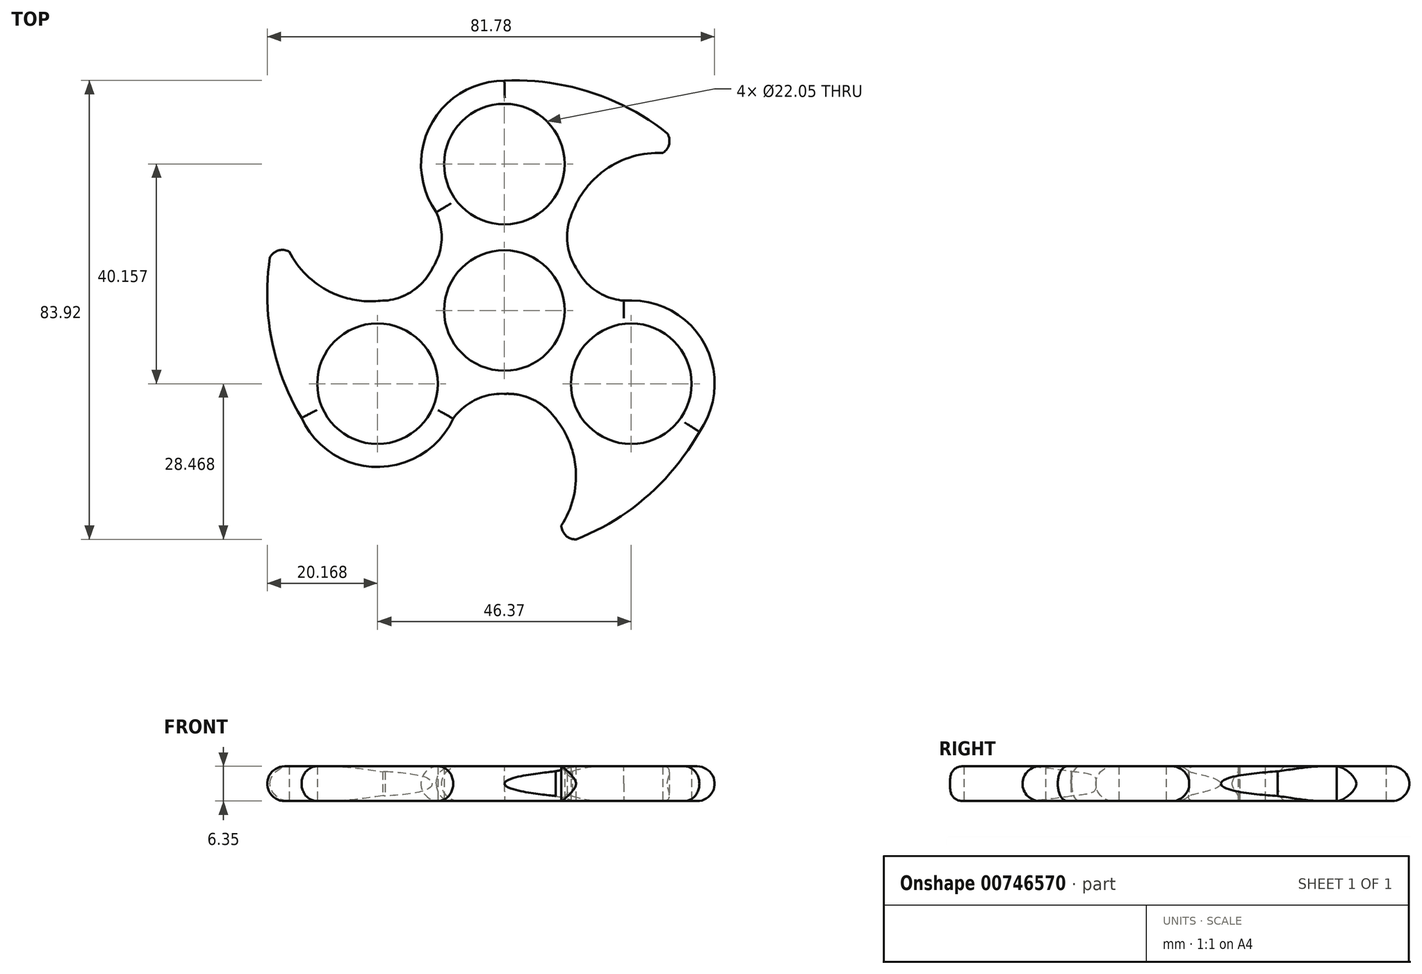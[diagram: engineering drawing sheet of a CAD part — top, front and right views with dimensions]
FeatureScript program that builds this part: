
annotation { "Feature Type Name" : "Feature", "Feature Type Description" : "" }
export const myFeature = defineFeature(function(context is Context, id is Id, definition is map)
    precondition{}
    {
        {
            var Q0;
            Q0=qCreatedBy(makeId("Top.planeOp"),FACE);
            var sketch = newSketch(context, id + "F0", { "sketchPlane" : qUnion([Q0])});
            skCircle(sketch, "E0", {"center": v(0, -0.08) * mm, "radius": 11.02 * mm});
            skCircle(sketch, "E1", {"center": v(0, -0.08) * mm, "radius": 15.24 * mm});
            skCircle(sketch, "E2", {"center": v(0, 26.7) * mm, "radius": 11.02 * mm});
            skCircle(sketch, "E3", {"center": v(0, 26.7) * mm, "radius": 15.24 * mm});
            skCircle(sketch, "E4.1.0", {"center": v(-23.2, -13.46) * mm, "radius": 15.24 * mm});
            skCircle(sketch, "E4.1.1", {"center": v(-23.2, -13.46) * mm, "radius": 11.02 * mm});
            skCircle(sketch, "E4.2.0", {"center": v(23.18, -13.46) * mm, "radius": 15.24 * mm});
            skCircle(sketch, "E4.2.1", {"center": v(23.18, -13.46) * mm, "radius": 11.02 * mm});
            skArc(sketch, "E5", {"start": v(0, -15.32) * mm, "mid": v(-5.27, -16.38) * mm, "end": v(-9.36, -19.86) * mm});
            skArc(sketch, "E6.MirrorCS", {"start": v(0, -15.32) * mm, "mid": v(5.25, -16.38) * mm, "end": v(9.35, -19.86) * mm});
            skArc(sketch, "E7.1.0", {"start": v(13.2, 7.54) * mm, "mid": v(11.48, 12.63) * mm, "end": v(12.45, 17.91) * mm});
            skArc(sketch, "E7.1.1", {"start": v(13.2, 7.54) * mm, "mid": v(16.75, 3.52) * mm, "end": v(21.8, 1.72) * mm});
            skArc(sketch, "E7.2.0", {"start": v(-13.2, 7.54) * mm, "mid": v(-16.76, 3.52) * mm, "end": v(-21.81, 1.72) * mm});
            skArc(sketch, "E7.2.1", {"start": v(-13.2, 7.54) * mm, "mid": v(-11.5, 12.63) * mm, "end": v(-12.46, 17.91) * mm});
            skLineSegment(sketch, "E7.anchor1", {"start": v(0, -0.08) * mm, "end": v(0.55, -26.06) * mm, "construction": true});
            skLineSegment(sketch, "E7.anchor2", {"start": v(0, -0.08) * mm, "end": v(-22.8, 12.43) * mm, "construction": true});
            skArc(sketch, "E8", {"start": v(35.18, 27.2) * mm, "mid": v(19.26, 38.54) * mm, "end": v(0, 41.94) * mm});
            skArc(sketch, "E9", {"start": v(35.18, 27.2) * mm, "mid": v(21.8, 27.5) * mm, "end": v(12.45, 17.91) * mm});
            skArc(sketch, "E10.1.0", {"start": v(-41.14, 16.87) * mm, "mid": v(-43, -2.6) * mm, "end": v(-36.32, -20.97) * mm});
            skArc(sketch, "E10.1.1", {"start": v(-41.14, 16.87) * mm, "mid": v(-34.72, 5.12) * mm, "end": v(-21.74, 1.82) * mm});
            skArc(sketch, "E10.2.0", {"start": v(5.96, -44.07) * mm, "mid": v(23.75, -35.94) * mm, "end": v(36.32, -20.97) * mm});
            skArc(sketch, "E10.2.1", {"start": v(5.96, -44.07) * mm, "mid": v(12.92, -32.63) * mm, "end": v(9.29, -19.74) * mm});
            skPoint(sketch, "E10.center", {"position": v(0, 0) * mm});
            skArc(sketch, "E11", {"start": v(-37.97, 8.47) * mm, "mid": v(-40.9, 10.98) * mm, "end": v(-43.1, 7.83) * mm});
            skArc(sketch, "E12.1.0", {"start": v(11.65, -37.12) * mm, "mid": v(10.93, -40.9) * mm, "end": v(14.77, -41.24) * mm});
            skArc(sketch, "E12.2.0", {"start": v(26.32, 28.65) * mm, "mid": v(29.96, 29.92) * mm, "end": v(28.33, 33.41) * mm});
            skSolve(sketch);
        }
        {
            var Q0;
            {var subQ0=sQuery(id+"F0.wireOp",EDGE,"E8");Q0=makeQuery(id+"F0.imprint","IMPRINT",FACE,{"disambiguationData":[TD([[makeQuery(id+"F0.imprint","IMPRINT",EDGE,{"derivedFrom":subQ0}),1.0]])]});}
            var Q1;
            Q1=makeQuery(id+"F0.imprint","IMPRINT",FACE,{"disambiguationData":[TD([[makeQuery(id+"F0.imprint","IMPRINT",EDGE,{"derivedFrom":sQuery(id+"F0.wireOp",EDGE,"E2")}),-1.0]])]});
            var Q2;
            Q2=makeQuery(id+"F0.imprint","IMPRINT",FACE,{"disambiguationData":[TD([[makeQuery(id+"F0.imprint","IMPRINT",EDGE,{"derivedFrom":sQuery(id+"F0.wireOp",EDGE,"E0")}),-1.0]])]});
            var Q3;
            {var subQ0=sQuery(id+"F0.wireOp",EDGE,"E7.1.0");var subQ1=sQuery(id+"F0.wireOp",EDGE,"E1");var subQ2=makeQuery(id+"F0.imprint","INTERSECT",VERTEX,{"derivedFrom":[subQ1,subQ0]});Q3=makeQuery(id+"F0.imprint","IMPRINT",FACE,{"disambiguationData":[TD([[makeQuery(id+"F0.imprint","IMPRINT",EDGE,{"disambiguationData":[TD([[subQ2,-1.0]])],"derivedFrom":subQ1}),-1.0]])]});}
            var Q4;
            {var subQ0=sQuery(id+"F0.wireOp",EDGE,"E3");var subQ1=sQuery(id+"F0.wireOp",EDGE,"E1");var subQ2=makeQuery(id+"F0.imprint","INTERSECT",VERTEX,{"disambiguationData":[OD(0.0)],"derivedFrom":[subQ1,subQ0]});Q4=makeQuery(id+"F0.imprint","IMPRINT",FACE,{"disambiguationData":[TD([[makeQuery(id+"F0.imprint","IMPRINT",EDGE,{"disambiguationData":[TD([[subQ2,-1.0]])],"derivedFrom":subQ1}),1.0]])]});}
            var Q5;
            {var subQ0=sQuery(id+"F0.wireOp",EDGE,"E7.2.1");var subQ1=sQuery(id+"F0.wireOp",EDGE,"E1");var subQ2=makeQuery(id+"F0.imprint","INTERSECT",VERTEX,{"derivedFrom":[subQ1,subQ0]});Q5=makeQuery(id+"F0.imprint","IMPRINT",FACE,{"disambiguationData":[TD([[makeQuery(id+"F0.imprint","IMPRINT",EDGE,{"disambiguationData":[TD([[subQ2,1.0]])],"derivedFrom":subQ1}),-1.0]])]});}
            var Q6;
            {var subQ0=sQuery(id+"F0.wireOp",EDGE,"E4.1.0");var subQ1=sQuery(id+"F0.wireOp",EDGE,"E1");var subQ2=makeQuery(id+"F0.imprint","INTERSECT",VERTEX,{"disambiguationData":[OD(0.0)],"derivedFrom":[subQ1,subQ0]});Q6=makeQuery(id+"F0.imprint","IMPRINT",FACE,{"disambiguationData":[TD([[makeQuery(id+"F0.imprint","IMPRINT",EDGE,{"disambiguationData":[TD([[subQ2,-1.0]])],"derivedFrom":subQ1}),1.0]])]});}
            var Q7;
            {var subQ0=sQuery(id+"F0.wireOp",EDGE,"E7.2.0");var subQ1=sQuery(id+"F0.wireOp",EDGE,"E1");var subQ2=makeQuery(id+"F0.imprint","INTERSECT",VERTEX,{"derivedFrom":[subQ1,subQ0]});Q7=makeQuery(id+"F0.imprint","IMPRINT",FACE,{"disambiguationData":[TD([[makeQuery(id+"F0.imprint","IMPRINT",EDGE,{"disambiguationData":[TD([[subQ2,-1.0]])],"derivedFrom":subQ1}),-1.0]])]});}
            var Q8;
            {var subQ0=sQuery(id+"F0.wireOp",EDGE,"E4.2.0");var subQ1=sQuery(id+"F0.wireOp",EDGE,"E1");var subQ2=makeQuery(id+"F0.imprint","INTERSECT",VERTEX,{"disambiguationData":[OD(0.0)],"derivedFrom":[subQ1,subQ0]});Q8=makeQuery(id+"F0.imprint","IMPRINT",FACE,{"disambiguationData":[TD([[makeQuery(id+"F0.imprint","IMPRINT",EDGE,{"disambiguationData":[TD([[subQ2,-1.0]])],"derivedFrom":subQ1}),1.0]])]});}
            var Q9;
            {var subQ0=sQuery(id+"F0.wireOp",EDGE,"E6.MirrorCS");var subQ1=sQuery(id+"F0.wireOp",EDGE,"E1");var subQ2=makeQuery(id+"F0.imprint","INTERSECT",VERTEX,{"derivedFrom":[subQ1,subQ0]});Q9=makeQuery(id+"F0.imprint","IMPRINT",FACE,{"disambiguationData":[TD([[makeQuery(id+"F0.imprint","IMPRINT",EDGE,{"disambiguationData":[TD([[subQ2,-1.0]])],"derivedFrom":subQ1}),-1.0]])]});}
            var Q10;
            {var subQ0=sQuery(id+"F0.wireOp",EDGE,"E5");var subQ1=sQuery(id+"F0.wireOp",EDGE,"E1");var subQ2=makeQuery(id+"F0.imprint","INTERSECT",VERTEX,{"derivedFrom":[subQ1,subQ0]});Q10=makeQuery(id+"F0.imprint","IMPRINT",FACE,{"disambiguationData":[TD([[makeQuery(id+"F0.imprint","IMPRINT",EDGE,{"disambiguationData":[TD([[subQ2,1.0]])],"derivedFrom":subQ1}),-1.0]])]});}
            var Q11;
            {var subQ0=sQuery(id+"F0.wireOp",EDGE,"E7.1.1");var subQ1=sQuery(id+"F0.wireOp",EDGE,"E1");var subQ2=makeQuery(id+"F0.imprint","INTERSECT",VERTEX,{"derivedFrom":[subQ1,subQ0]});Q11=makeQuery(id+"F0.imprint","IMPRINT",FACE,{"disambiguationData":[TD([[makeQuery(id+"F0.imprint","IMPRINT",EDGE,{"disambiguationData":[TD([[subQ2,1.0]])],"derivedFrom":subQ1}),-1.0]])]});}
            var Q12;
            Q12=makeQuery(id+"F0.imprint","IMPRINT",FACE,{"disambiguationData":[TD([[makeQuery(id+"F0.imprint","IMPRINT",EDGE,{"derivedFrom":sQuery(id+"F0.wireOp",EDGE,"E4.2.1")}),-1.0]])]});
            var Q13;
            {var subQ0=sQuery(id+"F0.wireOp",EDGE,"E10.2.0");var subQ1=sQuery(id+"F0.wireOp",EDGE,"E4.2.0");var subQ2=makeQuery(id+"F0.imprint","INTERSECT",VERTEX,{"derivedFrom":[subQ1,subQ0]});Q13=makeQuery(id+"F0.imprint","IMPRINT",FACE,{"disambiguationData":[TD([[makeQuery(id+"F0.imprint","IMPRINT",EDGE,{"disambiguationData":[TD([[subQ2,1.0]])],"derivedFrom":subQ1}),-1.0]])]});}
            var Q14;
            Q14=makeQuery(id+"F0.imprint","IMPRINT",FACE,{"disambiguationData":[TD([[makeQuery(id+"F0.imprint","IMPRINT",EDGE,{"derivedFrom":sQuery(id+"F0.wireOp",EDGE,"E4.1.1")}),-1.0]])]});
            var Q15;
            {var subQ0=sQuery(id+"F0.wireOp",EDGE,"E10.1.0");var subQ1=sQuery(id+"F0.wireOp",EDGE,"E4.1.0");var subQ2=makeQuery(id+"F0.imprint","INTERSECT",VERTEX,{"derivedFrom":[subQ1,subQ0]});Q15=makeQuery(id+"F0.imprint","IMPRINT",FACE,{"disambiguationData":[TD([[makeQuery(id+"F0.imprint","IMPRINT",EDGE,{"disambiguationData":[TD([[subQ2,1.0]])],"derivedFrom":subQ1}),-1.0]])]});}
            extrude(context, id + "F1", {"entities" : qUnion([Q0, Q1, Q2, Q3, Q4, Q5, Q6, Q7, Q8, Q9, Q10, Q11, Q12, Q13, Q14, Q15]), "depth" : 6.35 * mm, "offsetDistance" : 25.4 * mm});
        }
        {
            var Q0;
            Q0=makeQuery(id+"F1.opExtrude","CAP_EDGE",EDGE,{"disambiguationData":[OSD([sQuery(id+"F0.wireOp",EDGE,"E10.1.0")])],"isStart":false});
            var Q1;
            {var subQ0=sQuery(id+"F0.wireOp",EDGE,"E4.1.0");Q1=makeQuery(id+"F1.opExtrude","CAP_EDGE",EDGE,{"disambiguationData":[OSD([subQ0]),TDD([makeQuery(id+"F0.imprint","IMPRINT",EDGE,{"disambiguationData":[TD([[makeQuery(id+"F0.imprint","INTERSECT",VERTEX,{"derivedFrom":[subQ0,sQuery(id+"F0.wireOp",EDGE,"E5")]}),1.0]])],"derivedFrom":subQ0})])],"isStart":false});}
            var Q2;
            Q2=makeQuery(id+"F1.opExtrude","CAP_EDGE",EDGE,{"disambiguationData":[OSD([sQuery(id+"F0.wireOp",EDGE,"E5")])],"isStart":false});
            var Q3;
            Q3=makeQuery(id+"F1.opExtrude","CAP_EDGE",EDGE,{"disambiguationData":[OSD([sQuery(id+"F0.wireOp",EDGE,"E3")])],"isStart":false});
            var Q4;
            Q4=makeQuery(id+"F1.opExtrude","CAP_EDGE",EDGE,{"disambiguationData":[OSD([sQuery(id+"F0.wireOp",EDGE,"E8")])],"isStart":false});
            var Q5;
            Q5=makeQuery(id+"F1.opExtrude","CAP_EDGE",EDGE,{"disambiguationData":[OSD([sQuery(id+"F0.wireOp",EDGE,"E7.2.1")])],"isStart":false});
            var Q6;
            Q6=makeQuery(id+"F1.opExtrude","CAP_EDGE",EDGE,{"disambiguationData":[OSD([sQuery(id+"F0.wireOp",EDGE,"E7.1.1")])],"isStart":false});
            var Q7;
            {var subQ0=sQuery(id+"F0.wireOp",EDGE,"E4.2.0");Q7=makeQuery(id+"F1.opExtrude","CAP_EDGE",EDGE,{"disambiguationData":[OSD([subQ0]),TDD([makeQuery(id+"F0.imprint","IMPRINT",EDGE,{"disambiguationData":[TD([[makeQuery(id+"F0.imprint","INTERSECT",VERTEX,{"derivedFrom":[subQ0,sQuery(id+"F0.wireOp",EDGE,"E7.1.1")]}),1.0]])],"derivedFrom":subQ0})])],"isStart":false});}
            var Q8;
            Q8=makeQuery(id+"F1.opExtrude","CAP_EDGE",EDGE,{"disambiguationData":[OSD([sQuery(id+"F0.wireOp",EDGE,"E10.2.0")])],"isStart":false});
            fillet(context, id + "F2", {"entities" : qUnion([Q0, Q1, Q2, Q3, Q4, Q5, Q6, Q7, Q8]), "radius" : 3.17 * mm, "tangentPropagation" : true, "allowEdgeOverflow" : false});
        }
        {
            var Q0;
            {var subQ0=sQuery(id+"F0.wireOp",EDGE,"E4.1.0");Q0=makeQuery(id+"F1.opExtrude","CAP_EDGE",EDGE,{"disambiguationData":[OSD([subQ0]),TDD([makeQuery(id+"F0.imprint","IMPRINT",EDGE,{"disambiguationData":[TD([[makeQuery(id+"F0.imprint","INTERSECT",VERTEX,{"derivedFrom":[subQ0,sQuery(id+"F0.wireOp",EDGE,"E5")]}),1.0]])],"derivedFrom":subQ0})])],"isStart":true});}
            var Q1;
            Q1=makeQuery(id+"F1.opExtrude","CAP_EDGE",EDGE,{"disambiguationData":[OSD([sQuery(id+"F0.wireOp",EDGE,"E5")])],"isStart":true});
            var Q2;
            Q2=makeQuery(id+"F1.opExtrude","CAP_EDGE",EDGE,{"disambiguationData":[OSD([sQuery(id+"F0.wireOp",EDGE,"E10.1.0")])],"isStart":true});
            var Q3;
            Q3=makeQuery(id+"F1.opExtrude","CAP_EDGE",EDGE,{"disambiguationData":[OSD([sQuery(id+"F0.wireOp",EDGE,"E7.2.1")])],"isStart":true});
            var Q4;
            Q4=makeQuery(id+"F1.opExtrude","CAP_EDGE",EDGE,{"disambiguationData":[OSD([sQuery(id+"F0.wireOp",EDGE,"E3")])],"isStart":true});
            var Q5;
            Q5=makeQuery(id+"F1.opExtrude","CAP_EDGE",EDGE,{"disambiguationData":[OSD([sQuery(id+"F0.wireOp",EDGE,"E8")])],"isStart":true});
            var Q6;
            Q6=makeQuery(id+"F1.opExtrude","CAP_EDGE",EDGE,{"disambiguationData":[OSD([sQuery(id+"F0.wireOp",EDGE,"E7.1.1")])],"isStart":true});
            var Q7;
            {var subQ0=sQuery(id+"F0.wireOp",EDGE,"E4.2.0");Q7=makeQuery(id+"F1.opExtrude","CAP_EDGE",EDGE,{"disambiguationData":[OSD([subQ0]),TDD([makeQuery(id+"F0.imprint","IMPRINT",EDGE,{"disambiguationData":[TD([[makeQuery(id+"F0.imprint","INTERSECT",VERTEX,{"derivedFrom":[subQ0,sQuery(id+"F0.wireOp",EDGE,"E7.1.1")]}),1.0]])],"derivedFrom":subQ0})])],"isStart":true});}
            var Q8;
            Q8=makeQuery(id+"F1.opExtrude","CAP_EDGE",EDGE,{"disambiguationData":[OSD([sQuery(id+"F0.wireOp",EDGE,"E10.2.0")])],"isStart":true});
            fillet(context, id + "F3", {"entities" : qUnion([Q0, Q1, Q2, Q3, Q4, Q5, Q6, Q7, Q8]), "radius" : 3.17 * mm, "tangentPropagation" : true, "allowEdgeOverflow" : false});
        }
    });
